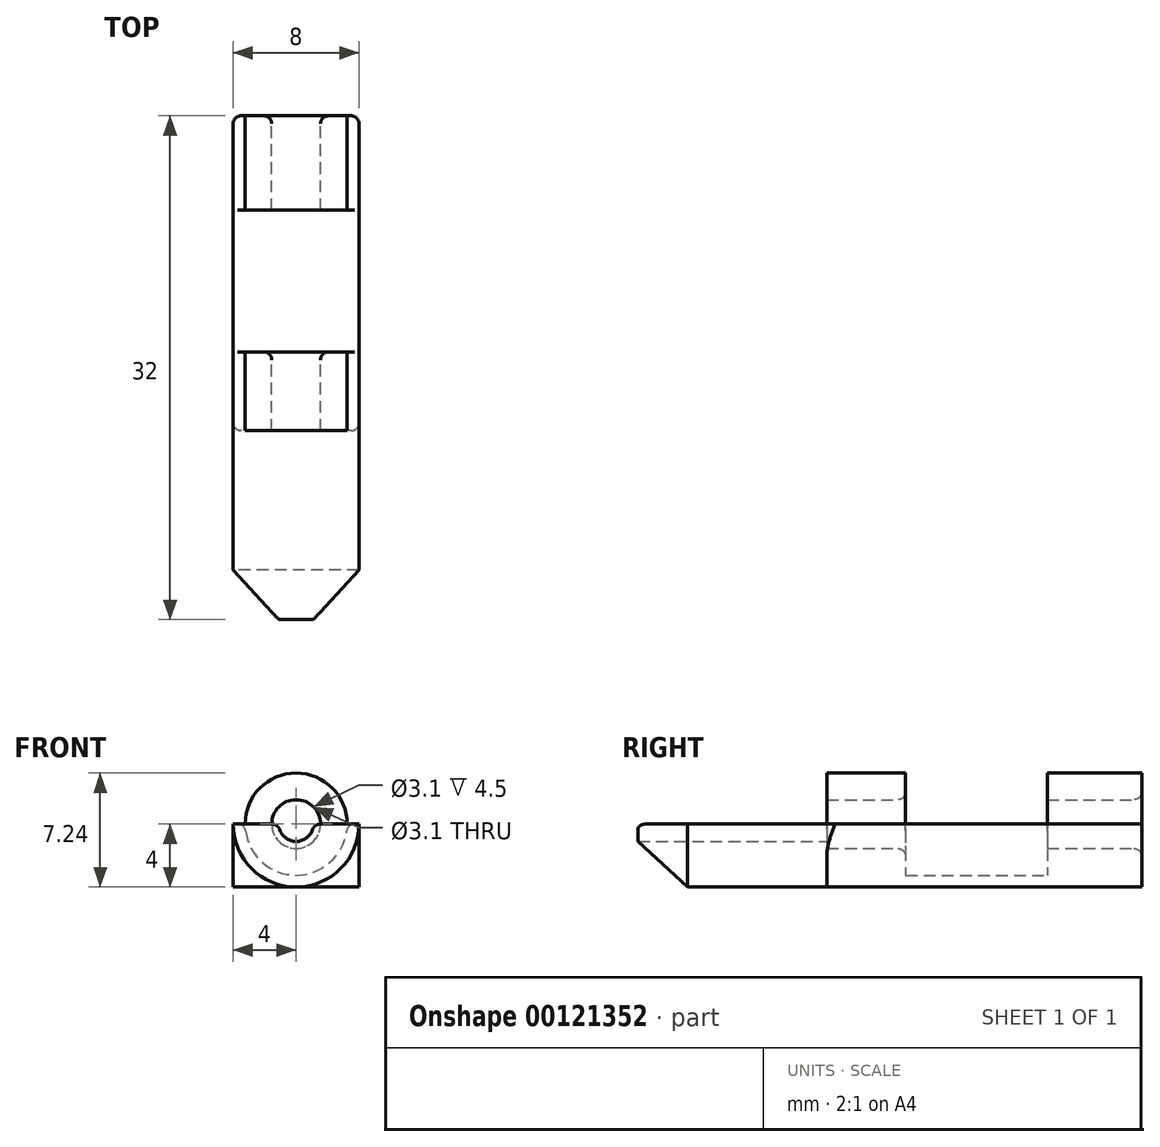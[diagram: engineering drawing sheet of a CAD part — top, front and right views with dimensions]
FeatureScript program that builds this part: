
annotation { "Feature Type Name" : "Feature", "Feature Type Description" : "" }
export const myFeature = defineFeature(function(context is Context, id is Id, definition is map)
    precondition{}
    {
        {
            var Q0;
            Q0=qCreatedBy(makeId("Top.planeOp"),FACE);
            var sketch = newSketch(context, id + "F0", { "sketchPlane" : qUnion([Q0])});
            skLineSegment(sketch, "E0", {"start": v(0, 20.85) * mm, "end": v(0, -12) * mm, "construction": true});
            skLineSegment(sketch, "E1", {"start": v(-4, 0) * mm, "end": v(7.04, 0) * mm, "construction": true});
            skLineSegment(sketch, "E2.0", {"start": v(-4.78, -12) * mm, "end": v(7.04, -12) * mm, "construction": true});
            skLineSegment(sketch, "E3.0", {"start": v(-1.1, 0) * mm, "end": v(-1.1, -12) * mm, "construction": true});
            skLineSegment(sketch, "E4.0", {"start": v(-1.55, 20.85) * mm, "end": v(-1.55, 0) * mm, "construction": true});
            skLineSegment(sketch, "E5.0", {"start": v(-4, 20.85) * mm, "end": v(-4, -12) * mm, "construction": true});
            skLineSegment(sketch, "E6", {"start": v(-1.1, -12) * mm, "end": v(-4, -8.86) * mm});
            skLineSegment(sketch, "E7", {"start": v(-4, -8.86) * mm, "end": v(-4, 0) * mm});
            skLineSegment(sketch, "E8", {"start": v(-1.55, 0) * mm, "end": v(-1.1, 0) * mm});
            skLineSegment(sketch, "E9", {"start": v(-1.1, -12) * mm, "end": v(-1.1, 0) * mm});
            skPoint(sketch, "E10.orphan", {"position": v(-4.78, 0) * mm});
            skLineSegment(sketch, "E11.0", {"start": v(-4, 20) * mm, "end": v(7.04, 20) * mm, "construction": true});
            skLineSegment(sketch, "E12.0", {"start": v(-4, 5) * mm, "end": v(7.04, 5) * mm, "construction": true});
            skLineSegment(sketch, "E13", {"start": v(-4, 0) * mm, "end": v(-1.1, 0) * mm});
            skLineSegment(sketch, "E14", {"start": v(-1.55, 5) * mm, "end": v(-4, 5) * mm});
            skLineSegment(sketch, "E15", {"start": v(-4, 0) * mm, "end": v(-4, 5) * mm});
            skLineSegment(sketch, "E16", {"start": v(-1.55, 5) * mm, "end": v(-1.55, 0) * mm});
            skLineSegment(sketch, "E17", {"start": v(-3.24, 5) * mm, "end": v(-3.24, 0) * mm});
            skLineSegment(sketch, "E18.0", {"start": v(-4, 14) * mm, "end": v(7.04, 14) * mm, "construction": true});
            skLineSegment(sketch, "E19", {"start": v(-3.24, 5) * mm, "end": v(-3.24, 14) * mm});
            skLineSegment(sketch, "E20", {"start": v(-3.24, 14) * mm, "end": v(-4, 14) * mm});
            skLineSegment(sketch, "E21", {"start": v(-4, 5) * mm, "end": v(-4, 14) * mm});
            skLineSegment(sketch, "E22", {"start": v(-3.24, 14) * mm, "end": v(-3.24, 20) * mm});
            skLineSegment(sketch, "E23", {"start": v(-3.24, 20) * mm, "end": v(-1.55, 20) * mm});
            skLineSegment(sketch, "E24", {"start": v(-1.55, 20) * mm, "end": v(-1.55, 14) * mm});
            skLineSegment(sketch, "E25", {"start": v(-1.55, 14) * mm, "end": v(-3.24, 14) * mm});
            skLineSegment(sketch, "E26", {"start": v(-3.24, 20) * mm, "end": v(-4, 20) * mm});
            skLineSegment(sketch, "E27", {"start": v(-4, 14) * mm, "end": v(-4, 20) * mm});
            skSolve(sketch);
        }
        {
            var Q0;
            Q0=makeQuery(id+"F0.imprint","IMPRINT",FACE,{"disambiguationData":[TD([[makeQuery(id+"F0.imprint","IMPRINT",EDGE,{"derivedFrom":sQuery(id+"F0.wireOp",EDGE,"E6")}),-1.0]])]});
            var Q1;
            {var subQ0=sQuery(id+"F0.wireOp",EDGE,"E15");Q1=makeQuery(id+"F0.imprint","IMPRINT",FACE,{"disambiguationData":[TD([[makeQuery(id+"F0.imprint","IMPRINT",EDGE,{"derivedFrom":subQ0}),-1.0]])]});}
            var Q2;
            {var subQ2=sQuery(id+"F0.wireOp",EDGE,"E19");Q2=makeQuery(id+"F0.imprint","IMPRINT",FACE,{"disambiguationData":[TD([[makeQuery(id+"F0.imprint","IMPRINT",EDGE,{"derivedFrom":subQ2}),1.0]])]});}
            var Q3;
            Q3=makeQuery(id+"F0.imprint","IMPRINT",FACE,{"disambiguationData":[TD([[makeQuery(id+"F0.imprint","IMPRINT",EDGE,{"derivedFrom":sQuery(id+"F0.wireOp",EDGE,"E20")}),-1.0]])]});
            var Q4;
            Q4=sQuery(id+"F0.wireOp",EDGE,"E0");
            revolve(context, id + "F1", {"entities" : qUnion([Q0, Q1, Q2, Q3]), "axis" : qUnion([Q4]), "revolveType" : RevolveType.ONE_DIRECTION, "angle" : 180 * degree});
        }
        {
            var Q0;
            {var subQ0=sQuery(id+"F0.wireOp",EDGE,"E16");Q0=makeQuery(id+"F0.imprint","IMPRINT",FACE,{"disambiguationData":[TD([[makeQuery(id+"F0.imprint","IMPRINT",EDGE,{"derivedFrom":subQ0}),-1.0]])]});}
            var Q1;
            Q1=makeQuery(id+"F0.imprint","IMPRINT",FACE,{"disambiguationData":[TD([[makeQuery(id+"F0.imprint","IMPRINT",EDGE,{"derivedFrom":sQuery(id+"F0.wireOp",EDGE,"E22")}),-1.0]])]});
            var Q2;
            Q2=sQuery(id+"F0.wireOp",EDGE,"E0");
            revolve(context, id + "F2", {"operationType" : NewBodyOperationType.ADD, "entities" : qUnion([Q0, Q1]), "axis" : qUnion([Q2]), "revolveType" : RevolveType.FULL});
        }
        {
            var Q0;
            Q0=makeQuery(id+"F2.boolean.opBoolean","MERGE",FACE,{"derivedFrom":[makeQuery(id+"F1.opRevolve","SWEPT_FACE",FACE,{"disambiguationData":[OSD([sQuery(id+"F0.wireOp",EDGE,"E26")])]}),makeQuery(id+"F2.opRevolve","SWEPT_FACE",FACE,{"disambiguationData":[OSD([sQuery(id+"F0.wireOp",EDGE,"E23")])]})]});
            var sketch = newSketch(context, id + "F3", { "sketchPlane" : qUnion([Q0])});
            skArc(sketch, "E28.0.0", {"start": v(-4, 0) * mm, "mid": v(0, -4) * mm, "end": v(4, 0) * mm});
            skLineSegment(sketch, "E28.0.1", {"start": v(4, 0) * mm, "end": v(3.24, 0) * mm});
            skArc(sketch, "E28.0.2", {"start": v(3.24, 0) * mm, "mid": v(0, 3.24) * mm, "end": v(-3.24, 0) * mm});
            skLineSegment(sketch, "E28.0.3", {"start": v(-3.24, 0) * mm, "end": v(-4, 0) * mm});
            skLineSegment(sketch, "E29", {"start": v(-4, 0) * mm, "end": v(-4, -4) * mm});
            skPoint(sketch, "E29.endSnap0", {"position": v(0, -4) * mm});
            skLineSegment(sketch, "E30", {"start": v(-4, -4) * mm, "end": v(4, -4) * mm});
            skLineSegment(sketch, "E31", {"start": v(4, -4) * mm, "end": v(4, 0) * mm});
            skSolve(sketch);
        }
        {
            var Q0;
            {var subQ0=sQuery(id+"F3.wireOp",EDGE,"E29");Q0=makeQuery(id+"F3.imprint","IMPRINT",FACE,{"disambiguationData":[TD([[makeQuery(id+"F3.imprint","IMPRINT",EDGE,{"derivedFrom":subQ0}),1.0]])]});}
            var Q1;
            {var subQ0=sQuery(id+"F3.wireOp",EDGE,"E31");Q1=makeQuery(id+"F3.imprint","IMPRINT",FACE,{"disambiguationData":[TD([[makeQuery(id+"F3.imprint","IMPRINT",EDGE,{"derivedFrom":subQ0}),1.0]])]});}
            extrude(context, id + "F4", {"entities" : qUnion([Q0, Q1]), "operationType" : NewBodyOperationType.ADD, "oppositeDirection" : true, "depth" : 20 * mm});
        }
        {
            var Q0;
            Q0=makeQuery(id+"F1.opRevolve","CAP_EDGE",EDGE,{"disambiguationData":[OSD([sQuery(id+"F0.wireOp",EDGE,"E9")])],"isStart":false});
            var Q1;
            Q1=makeQuery(id+"F1.opRevolve","CAP_EDGE",EDGE,{"disambiguationData":[OSD([sQuery(id+"F0.wireOp",EDGE,"E9")])],"isStart":true});
            var Q2;
            Q2=makeQuery(id+"F2.opRevolve","SWEPT_EDGE",EDGE,{"disambiguationData":[OSD([sQuery(id+"F0.wireOp",EDGE,"E14"),sQuery(id+"F0.wireOp",EDGE,"E16")])]});
            var Q3;
            Q3=makeQuery(id+"F2.opRevolve","SWEPT_EDGE",EDGE,{"disambiguationData":[OSD([sQuery(id+"F0.wireOp",EDGE,"E23"),sQuery(id+"F0.wireOp",EDGE,"E24")])]});
            var Q4;
            {var subQ0=sQuery(id+"F0.wireOp",EDGE,"E22");var subQ1=sQuery(id+"F0.wireOp",EDGE,"E19");var subQ2=sQuery(id+"F0.wireOp",EDGE,"E17");Q4=makeQuery(id+"F2.boolean.opBoolean","SPLIT",EDGE,{"disambiguationData":[topologyDisambiguationEdgeConnected([makeQuery(id+"F1.opRevolve","SWEPT_FACE",FACE,{"disambiguationData":[OSD([subQ2,subQ1,subQ0])]})])],"derivedFrom":makeQuery(id+"F1.opRevolve","CAP_EDGE",EDGE,{"disambiguationData":[OSD([subQ2,subQ1,subQ0])],"isStart":false})});}
            var Q5;
            {var subQ0=sQuery(id+"F0.wireOp",EDGE,"E22");var subQ1=sQuery(id+"F0.wireOp",EDGE,"E19");var subQ2=sQuery(id+"F0.wireOp",EDGE,"E17");Q5=makeQuery(id+"F2.boolean.opBoolean","SPLIT",EDGE,{"disambiguationData":[topologyDisambiguationEdgeConnected([makeQuery(id+"F1.opRevolve","SWEPT_FACE",FACE,{"disambiguationData":[OSD([subQ2,subQ1,subQ0])]})])],"derivedFrom":makeQuery(id+"F1.opRevolve","CAP_EDGE",EDGE,{"disambiguationData":[OSD([subQ2,subQ1,subQ0])],"isStart":true})});}
            var Q6;
            Q6=makeQuery(id+"F4.opExtrude","CAP_EDGE",EDGE,{"disambiguationData":[OSD([sQuery(id+"F3.wireOp",EDGE,"E29")])],"isStart":true});
            var Q7;
            Q7=makeQuery(id+"F4.opExtrude","CAP_EDGE",EDGE,{"disambiguationData":[OSD([sQuery(id+"F3.wireOp",EDGE,"E31")])],"isStart":true});
            var Q8;
            Q8=makeQuery(id+"F4.opExtrude","CAP_EDGE",EDGE,{"disambiguationData":[OSD([sQuery(id+"F3.wireOp",EDGE,"E29")])],"isStart":false});
            var Q9;
            Q9=makeQuery(id+"F4.opExtrude","CAP_EDGE",EDGE,{"disambiguationData":[OSD([sQuery(id+"F3.wireOp",EDGE,"E31")])],"isStart":false});
            fillet(context, id + "F5", {"entities" : qUnion([Q0, Q1, Q2, Q3, Q4, Q5, Q6, Q7, Q8, Q9]), "radius" : .5 * mm, "tangentPropagation" : true, "allowEdgeOverflow" : false});
        }
    });
